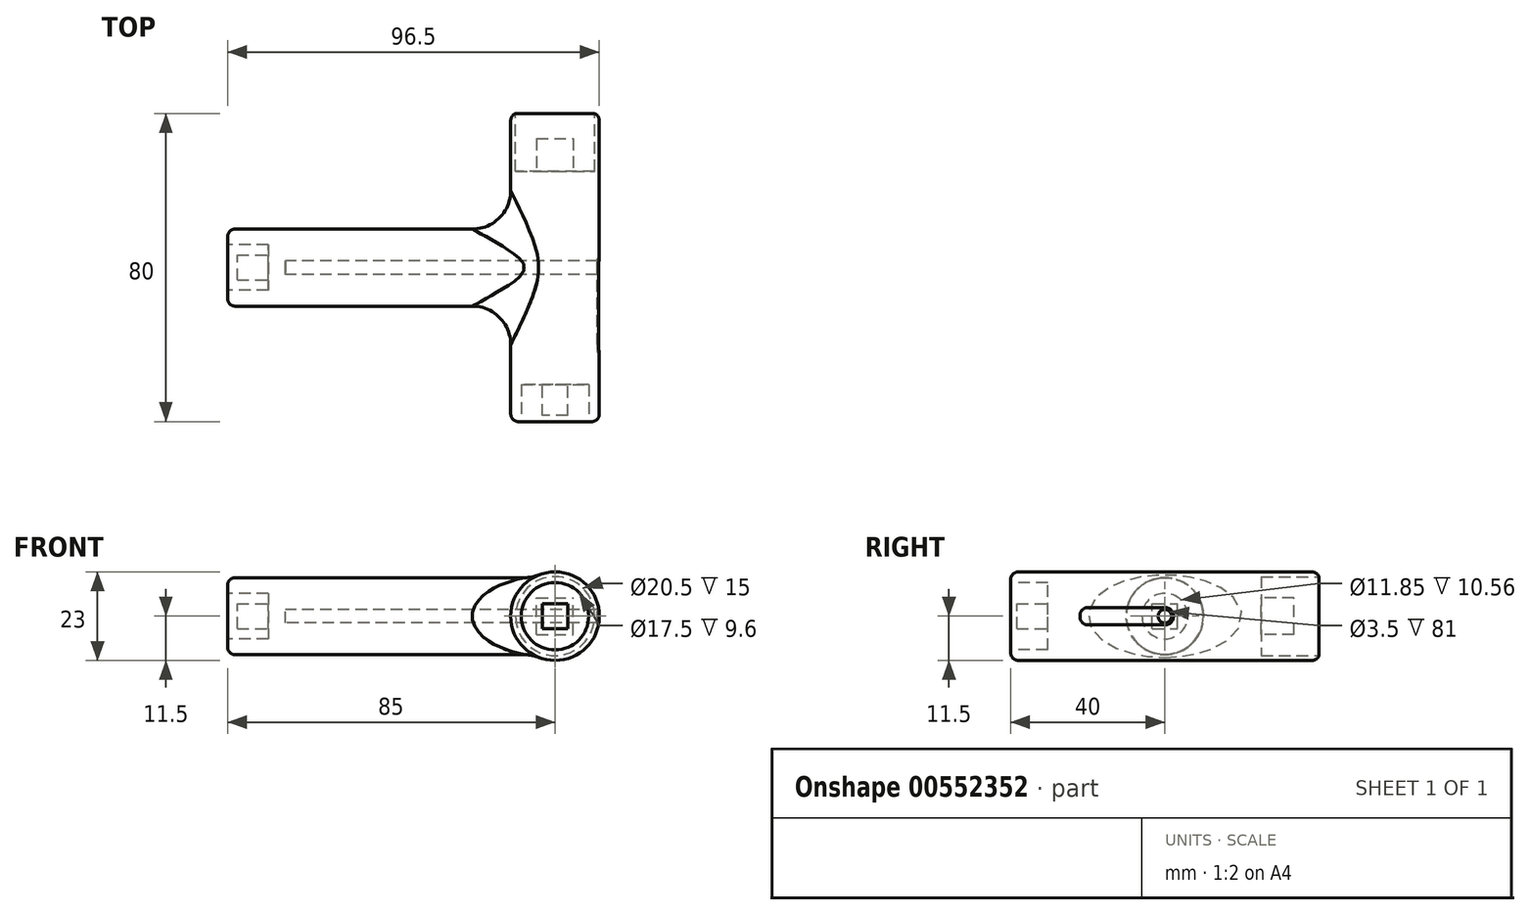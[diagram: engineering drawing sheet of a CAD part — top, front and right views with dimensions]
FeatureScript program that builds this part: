
annotation { "Feature Type Name" : "Feature", "Feature Type Description" : "" }
export const myFeature = defineFeature(function(context is Context, id is Id, definition is map)
    precondition{}
    {
        {
            var Q0;
            Q0=qCreatedBy(makeId("Front.planeOp"),FACE);
            var sketch = newSketch(context, id + "F0", { "sketchPlane" : qUnion([Q0])});
            skCircle(sketch, "E0", {"center": v(0, 0) * mm, "radius": 11.5 * mm});
            skSolve(sketch);
        }
        {
            var Q0;
            Q0=makeQuery(id+"F0.imprint","IMPRINT",FACE,{"disambiguationData":[TD([[makeQuery(id+"F0.imprint","IMPRINT",EDGE,{"derivedFrom":sQuery(id+"F0.wireOp",EDGE,"E0")}),1.0]])]});
            extrude(context, id + "F1", {"entities" : qUnion([Q0]), "endBound" : BoundingType.SYMMETRIC, "depth" : 80 * mm, "offsetDistance" : 25 * mm});
        }
        {
            var Q0;
            Q0=qCreatedBy(makeId("Right.planeOp"),FACE);
            var sketch = newSketch(context, id + "F2", { "sketchPlane" : qUnion([Q0])});
            skCircle(sketch, "E1", {"center": v(0, 0) * mm, "radius": 10 * mm});
            skSolve(sketch);
        }
        {
            var Q0;
            Q0 = qSketchRegion(id + "F2", true);
            extrude(context, id + "F3", {"entities" : qUnion([Q0]), "operationType" : NewBodyOperationType.ADD, "oppositeDirection" : true, "depth" : 85 * mm, "offsetDistance" : 25 * mm});
        }
        {
            var Q0;
            Q0=makeQuery(id+"F1.opExtrude","CAP_FACE",FACE,{"disambiguationData":[OSD([sQuery(id+"F0.wireOp",EDGE,"E0")])],"isStart":true});
            var sketch = newSketch(context, id + "F4", { "sketchPlane" : qUnion([Q0])});
            skCircle(sketch, "E2", {"center": v(0, 0) * mm, "radius": 10.25 * mm});
            skSolve(sketch);
        }
        {
            var Q0;
            Q0=makeQuery(id+"F4.imprint","IMPRINT",FACE,{"disambiguationData":[TD([[makeQuery(id+"F4.imprint","IMPRINT",EDGE,{"derivedFrom":sQuery(id+"F4.wireOp",EDGE,"E2")}),1.0]])]});
            extrude(context, id + "F5", {"entities" : qUnion([Q0]), "operationType" : NewBodyOperationType.REMOVE, "oppositeDirection" : true, "depth" : 15 * mm, "offsetDistance" : 25 * mm});
        }
        {
            var Q0;
            Q0=makeQuery(id+"F1.opExtrude","CAP_FACE",FACE,{"disambiguationData":[OSD([sQuery(id+"F0.wireOp",EDGE,"E0")])],"isStart":false});
            var sketch = newSketch(context, id + "F6", { "sketchPlane" : qUnion([Q0])});
            skCircle(sketch, "E3", {"center": v(0, 0) * mm, "radius": 8.75 * mm});
            skSolve(sketch);
        }
        {
            var Q0;
            Q0=makeQuery(id+"F6.imprint","IMPRINT",FACE,{"disambiguationData":[TD([[makeQuery(id+"F6.imprint","IMPRINT",EDGE,{"derivedFrom":sQuery(id+"F6.wireOp",EDGE,"E3")}),1.0]])]});
            extrude(context, id + "F7", {"entities" : qUnion([Q0]), "operationType" : NewBodyOperationType.REMOVE, "oppositeDirection" : true, "depth" : 9.6 * mm, "offsetDistance" : 25 * mm});
        }
        {
            var Q0;
            Q0=makeQuery(id+"F3.opExtrude","CAP_FACE",FACE,{"disambiguationData":[OSD([sQuery(id+"F2.wireOp",EDGE,"E1")])],"isStart":false});
            var sketch = newSketch(context, id + "F8", { "sketchPlane" : qUnion([Q0])});
            skCircle(sketch, "E4", {"center": v(0, 0) * mm, "radius": 5.92 * mm});
            skSolve(sketch);
        }
        {
            var Q0;
            Q0=makeQuery(id+"F8.imprint","IMPRINT",FACE,{"disambiguationData":[TD([[makeQuery(id+"F8.imprint","IMPRINT",EDGE,{"derivedFrom":sQuery(id+"F8.wireOp",EDGE,"E4")}),1.0]])]});
            extrude(context, id + "F9", {"entities" : qUnion([Q0]), "operationType" : NewBodyOperationType.REMOVE, "oppositeDirection" : true, "depth" : 10.56 * mm, "offsetDistance" : 25 * mm});
        }
        {
            var Q0;
            Q0=makeQuery(id+"F5.boolean.opBoolean","COPY",FACE,{"derivedFrom":makeQuery(id+"F5.opExtrude","CAP_FACE",FACE,{"disambiguationData":[OSD([sQuery(id+"F4.wireOp",EDGE,"E2")])],"isStart":false})});
            var sketch = newSketch(context, id + "F10", { "sketchPlane" : qUnion([Q0])});
            skLineSegment(sketch, "E5.bottom", {"start": v(4.75, -4.75) * mm, "end": v(-4.75, -4.75) * mm});
            skLineSegment(sketch, "E5.top", {"start": v(4.75, 4.75) * mm, "end": v(-4.75, 4.75) * mm});
            skLineSegment(sketch, "E5.left", {"start": v(4.75, -4.75) * mm, "end": v(4.75, 4.75) * mm});
            skLineSegment(sketch, "E5.right", {"start": v(-4.75, -4.75) * mm, "end": v(-4.75, 4.75) * mm});
            skPoint(sketch, "E5.middle", {"position": v(0, 0) * mm});
            skSolve(sketch);
        }
        {
            var Q0;
            Q0=makeQuery(id+"F10.imprint","IMPRINT",FACE,{"disambiguationData":[TD([[makeQuery(id+"F10.imprint","IMPRINT",EDGE,{"derivedFrom":sQuery(id+"F10.wireOp",EDGE,"E5.bottom")}),-1.0]])]});
            extrude(context, id + "F11", {"entities" : qUnion([Q0]), "operationType" : NewBodyOperationType.ADD, "depth" : 8.5 * mm, "offsetDistance" : 25 * mm});
        }
        {
            var Q0;
            Q0=makeQuery(id+"F9.boolean.opBoolean","COPY",FACE,{"derivedFrom":makeQuery(id+"F9.opExtrude","CAP_FACE",FACE,{"disambiguationData":[OSD([sQuery(id+"F8.wireOp",EDGE,"E4")])],"isStart":false})});
            var sketch = newSketch(context, id + "F12", { "sketchPlane" : qUnion([Q0])});
            skLineSegment(sketch, "E6.bottom", {"start": v(3.25, -3.25) * mm, "end": v(-3.25, -3.25) * mm});
            skLineSegment(sketch, "E6.top", {"start": v(3.25, 3.25) * mm, "end": v(-3.25, 3.25) * mm});
            skLineSegment(sketch, "E6.left", {"start": v(3.25, -3.25) * mm, "end": v(3.25, 3.25) * mm});
            skLineSegment(sketch, "E6.right", {"start": v(-3.25, -3.25) * mm, "end": v(-3.25, 3.25) * mm});
            skPoint(sketch, "E6.middle", {"position": v(0, 0) * mm});
            skSolve(sketch);
        }
        {
            var Q0;
            Q0=makeQuery(id+"F12.imprint","IMPRINT",FACE,{"disambiguationData":[TD([[makeQuery(id+"F12.imprint","IMPRINT",EDGE,{"derivedFrom":sQuery(id+"F12.wireOp",EDGE,"E6.bottom")}),-1.0]])]});
            extrude(context, id + "F13", {"entities" : qUnion([Q0]), "operationType" : NewBodyOperationType.ADD, "depth" : 8 * mm, "offsetDistance" : 25 * mm});
        }
        {
            var Q0;
            Q0=makeQuery(id+"F7.boolean.opBoolean","COPY",FACE,{"derivedFrom":makeQuery(id+"F7.opExtrude","CAP_FACE",FACE,{"disambiguationData":[OSD([sQuery(id+"F6.wireOp",EDGE,"E3")])],"isStart":false})});
            var sketch = newSketch(context, id + "F14", { "sketchPlane" : qUnion([Q0])});
            skLineSegment(sketch, "E7.bottom", {"start": v(3.25, -3.25) * mm, "end": v(-3.25, -3.25) * mm});
            skLineSegment(sketch, "E7.top", {"start": v(3.25, 3.25) * mm, "end": v(-3.25, 3.25) * mm});
            skLineSegment(sketch, "E7.left", {"start": v(3.25, -3.25) * mm, "end": v(3.25, 3.25) * mm});
            skLineSegment(sketch, "E7.right", {"start": v(-3.25, -3.25) * mm, "end": v(-3.25, 3.25) * mm});
            skPoint(sketch, "E7.middle", {"position": v(0, 0) * mm});
            skSolve(sketch);
        }
        {
            var Q0;
            Q0=makeQuery(id+"F14.imprint","IMPRINT",FACE,{"disambiguationData":[TD([[makeQuery(id+"F14.imprint","IMPRINT",EDGE,{"derivedFrom":sQuery(id+"F14.wireOp",EDGE,"E7.bottom")}),-1.0]])]});
            extrude(context, id + "F15", {"entities" : qUnion([Q0]), "operationType" : NewBodyOperationType.ADD, "depth" : 8 * mm, "offsetDistance" : 25 * mm});
        }
        {
            var Q0;
            Q0=makeQuery(id+"F3.boolean.opBoolean","INTERSECT",EDGE,{"derivedFrom":[makeQuery(id+"F1.opExtrude","SWEPT_FACE",FACE,{"disambiguationData":[OSD([sQuery(id+"F0.wireOp",EDGE,"E0")])]}),makeQuery(id+"F3.opExtrude","SWEPT_FACE",FACE,{"disambiguationData":[OSD([sQuery(id+"F2.wireOp",EDGE,"E1")])]})]});
            fillet(context, id + "F16", {"entities" : qUnion([Q0]), "radius" : 10 * mm, "tangentPropagation" : true, "allowEdgeOverflow" : false});
        }
        {
            var Q0;
            Q0=makeQuery(id+"F3.opExtrude","CAP_EDGE",EDGE,{"disambiguationData":[OSD([sQuery(id+"F2.wireOp",EDGE,"E1")])],"isStart":false});
            var Q1;
            Q1=makeQuery(id+"F1.opExtrude","CAP_EDGE",EDGE,{"disambiguationData":[OSD([sQuery(id+"F0.wireOp",EDGE,"E0")])],"isStart":true});
            var Q2;
            Q2=makeQuery(id+"F1.opExtrude","CAP_EDGE",EDGE,{"disambiguationData":[OSD([sQuery(id+"F0.wireOp",EDGE,"E0")])],"isStart":false});
            fillet(context, id + "F17", {"entities" : qUnion([Q0, Q1, Q2]), "radius" : 2 * mm, "tangentPropagation" : true, "allowEdgeOverflow" : false});
        }
        {
            var Q0;
            Q0=qCreatedBy(makeId("Right.planeOp"),FACE);
            var sketch = newSketch(context, id + "F18", { "sketchPlane" : qUnion([Q0])});
            skCircle(sketch, "E8", {"center": v(0, 0) * mm, "radius": 1.75 * mm});
            skSolve(sketch);
        }
        {
            var Q0;
            Q0 = qSketchRegion(id + "F18", true);
            extrude(context, id + "F19", {"entities" : qUnion([Q0]), "operationType" : NewBodyOperationType.REMOVE, "depth" : 14 * mm, "offsetDistance" : 25 * mm});
        }
        {
            var Q0;
            Q0=makeQuery(id+"F19.boolean.opBoolean","COPY",FACE,{"derivedFrom":makeQuery(id+"F19.opExtrude","CAP_FACE",FACE,{"disambiguationData":[OSD([sQuery(id+"F18.wireOp",EDGE,"E8")])],"isStart":true})});
            var sketch = newSketch(context, id + "F20", { "sketchPlane" : qUnion([Q0])});
            skCircle(sketch, "E9", {"center": v(0, 0) * mm, "radius": 1.75 * mm});
            skSolve(sketch);
        }
        {
            var Q0;
            Q0=makeQuery(id+"F20.imprint","IMPRINT",FACE,{"disambiguationData":[TD([[makeQuery(id+"F20.imprint","IMPRINT",EDGE,{"derivedFrom":sQuery(id+"F20.wireOp",EDGE,"E9")}),1.0]])]});
            extrude(context, id + "F21", {"entities" : qUnion([Q0]), "operationType" : NewBodyOperationType.REMOVE, "oppositeDirection" : true, "depth" : 70 * mm, "offsetDistance" : 25 * mm});
        }
        {
            var Q0;
            Q0=qCreatedBy(makeId("Right.planeOp"),FACE);
            var sketch = newSketch(context, id + "F22", { "sketchPlane" : qUnion([Q0])});
            skLineSegment(sketch, "E10.bottom", {"start": v(-22, -2.25) * mm, "end": v(0, -2.25) * mm});
            skLineSegment(sketch, "E10.top", {"start": v(-22, 2.25) * mm, "end": v(0, 2.25) * mm});
            skLineSegment(sketch, "E10.left", {"start": v(-22, -2.25) * mm, "end": v(-22, 2.25) * mm});
            skPoint(sketch, "E10.middle", {"position": v(0, 0) * mm});
            skPoint(sketch, "E11", {"position": v(0, 2.25) * mm});
            skPoint(sketch, "E12", {"position": v(0, -2.25) * mm});
            skArc(sketch, "E13", {"start": v(-0.16, -2.25) * mm, "mid": v(2.26, 0) * mm, "end": v(-0.16, 2.25) * mm});
            skSolve(sketch);
        }
        {
            var Q0;
            Q0 = qSketchRegion(id + "F22", true);
            extrude(context, id + "F23", {"entities" : qUnion([Q0]), "operationType" : NewBodyOperationType.REMOVE, "depth" : 13.6 * mm, "offsetDistance" : 25 * mm});
        }
        {
            var Q0;
            Q0=makeQuery(id+"F23.boolean.opBoolean","COPY",FACE,{"derivedFrom":makeQuery(id+"F23.opExtrude","CAP_FACE",FACE,{"disambiguationData":[OSD([sQuery(id+"F22.wireOp",EDGE,"E10.bottom"),sQuery(id+"F22.wireOp",EDGE,"E10.top"),sQuery(id+"F22.wireOp",EDGE,"E10.left"),sQuery(id+"F22.wireOp",EDGE,"E13")])],"isStart":true})});
            extrude(context, id + "F24", {"entities" : qUnion([Q0]), "operationType" : NewBodyOperationType.ADD, "depth" : 11 * mm, "offsetDistance" : 25 * mm});
        }
        {
            var Q0;
            Q0=makeQuery(id+"F23.boolean.opBoolean","COPY",EDGE,{"derivedFrom":makeQuery(id+"F23.opExtrude","SWEPT_EDGE",EDGE,{"disambiguationData":[OSD([sQuery(id+"F22.wireOp",EDGE,"E10.bottom"),sQuery(id+"F22.wireOp",EDGE,"E10.left")])]})});
            var Q1;
            Q1=makeQuery(id+"F23.boolean.opBoolean","COPY",EDGE,{"derivedFrom":makeQuery(id+"F23.opExtrude","SWEPT_EDGE",EDGE,{"disambiguationData":[OSD([sQuery(id+"F22.wireOp",EDGE,"E10.top"),sQuery(id+"F22.wireOp",EDGE,"E10.left")])]})});
            fillet(context, id + "F25", {"entities" : qUnion([Q0, Q1]), "radius" : 2 * mm, "tangentPropagation" : true, "allowEdgeOverflow" : false});
        }
    });
